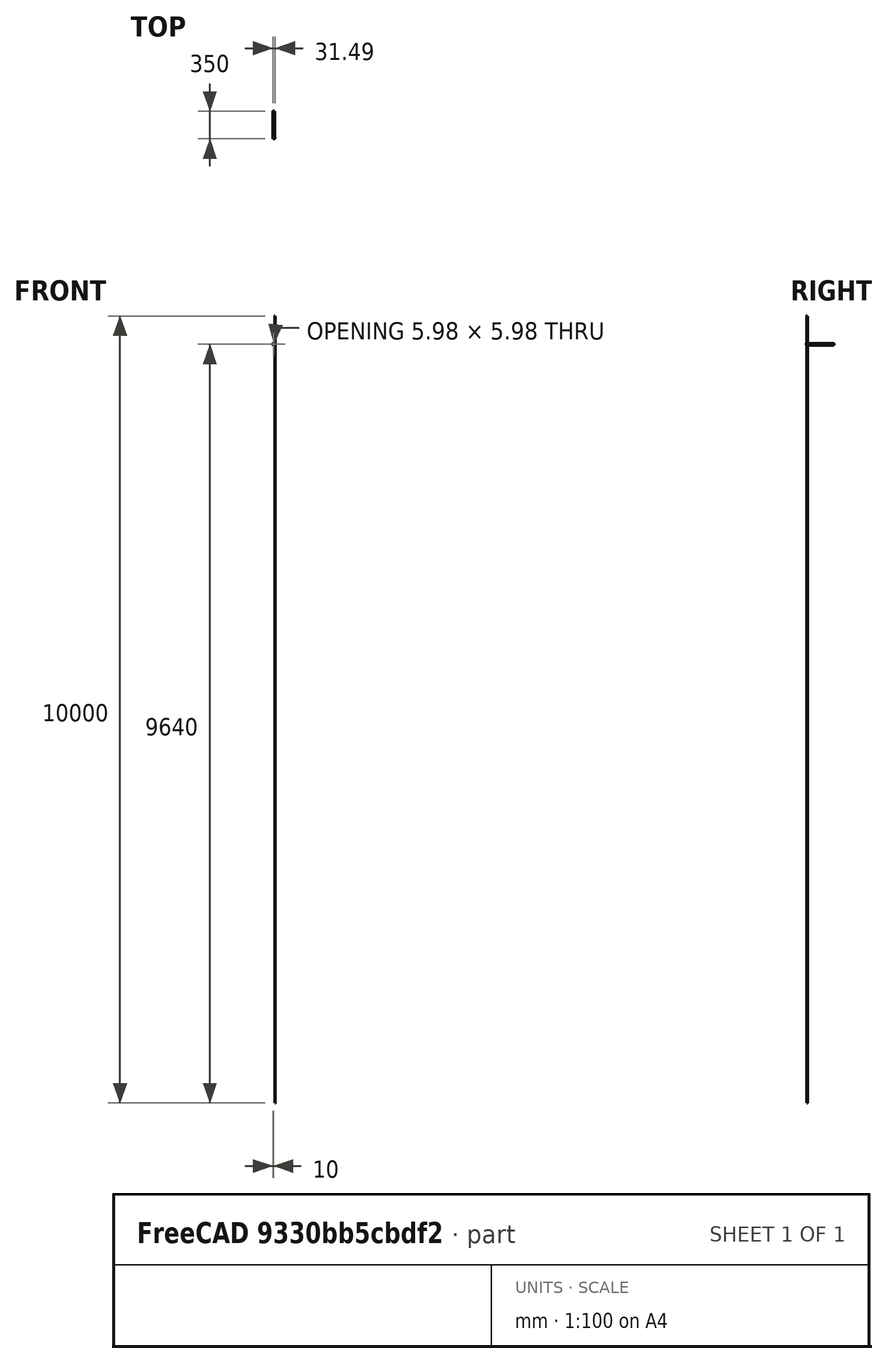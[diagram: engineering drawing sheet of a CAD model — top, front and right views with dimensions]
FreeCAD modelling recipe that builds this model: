
FCSTD DOCUMENT  (FreeCAD 0.14R3703 (Git))
Label: perfiles_horizontales_Y
License: CC-BY 3.0
LicenseURL: http://creativecommons.org/licenses/by/3.0/
objects: Sketcher::SketchObject×2, PartDesign::Pad×1, PartDesign::Pocket×1, Part::Feature×1
note: 7 computed .brp shape members not serialized (recipe doc carries the construction recipe); baked Part::Feature solids carry a one-line shape summary decoded from their .brp

FEATURE [Sketcher::SketchObject] Sketch
  Placement = pos=(0,0,-1.5) rot=(-0.57735,0.57735,0.57735;2.0944rad)
  sketch-geometry (136):
    g0: LineSegment StartX=0 StartY=20 StartZ=0 EndX=4.65 EndY=20 EndZ=0
    g1: ArcOfCircle CenterX=-1e-12 CenterY=18.5 CenterZ=0 NormalX=0 NormalY=0 NormalZ=1 Radius=1.5 StartAngle=1.5708 EndAngle=3.14159
    g2: LineSegment StartX=-1.5 StartY=13.85 StartZ=0 EndX=-1.5 EndY=18.5 EndZ=0
    g3: ArcOfCircle CenterX=-1.3 CenterY=13.85 CenterZ=0 NormalX=0 NormalY=0 NormalZ=1 Radius=0.2 StartAngle=3.14159 EndAngle=4.71239
    g4: LineSegment StartX=-1 StartY=13.65 StartZ=0 EndX=-1.3 EndY=13.65 EndZ=0
    g5: LineSegment StartX=-1 StartY=13.3 StartZ=0 EndX=-1 EndY=13.65 EndZ=0
    g6: ArcOfCircle CenterX=-0.8 CenterY=13.3 CenterZ=0 NormalX=0 NormalY=0 NormalZ=1 Radius=0.2 StartAngle=3.14159 EndAngle=4.71239
    g7: LineSegment StartX=-0.5 StartY=13.1 StartZ=0 EndX=-0.8 EndY=13.1 EndZ=0
    g8: ArcOfCircle CenterX=-0.5 CenterY=13.6 CenterZ=0 NormalX=0 NormalY=0 NormalZ=1 Radius=0.5 StartAngle=4.71239 EndAngle=6.28319
    g9: LineSegment StartX=2.68e-07 StartY=15.5 StartZ=0 EndX=2.68e-07 EndY=13.6 EndZ=0
    g10: ArcOfCircle CenterX=0.5 CenterY=15.5 CenterZ=0 NormalX=0 NormalY=0 NormalZ=1 Radius=0.5 StartAngle=1.5708 EndAngle=3.14159
    g11: LineSegment StartX=1.23223 StartY=16 StartZ=0 EndX=0.5 EndY=16 EndZ=0
    g12: ArcOfCircle CenterX=1.23223 CenterY=15.5 CenterZ=0 NormalX=0 NormalY=0 NormalZ=1 Radius=0.5 StartAngle=0.785398 EndAngle=1.5708
    g13: LineSegment StartX=3.85355 StartY=13.5858 StartZ=0 EndX=1.58579 EndY=15.8536 EndZ=0
    g14: ArcOfCircle CenterX=3.5 CenterY=13.2322 CenterZ=0 NormalX=0 NormalY=0 NormalZ=1 Radius=0.5 StartAngle=0 EndAngle=0.785398
    g15: LineSegment StartX=4 StartY=10.9536 StartZ=0 EndX=4 EndY=13.2322 EndZ=0
    g16: ArcOfCircle CenterX=4.2 CenterY=10.9536 CenterZ=0 NormalX=0 NormalY=0 NormalZ=1 Radius=0.2 StartAngle=3.14159 EndAngle=3.66519
    g17: LineSegment StartX=4.46188 StartY=10.1 StartZ=0 EndX=4.0268 EndY=10.8536 EndZ=0
    g18: ArcOfCircle CenterX=4.28868 CenterY=10 CenterZ=0 NormalX=0 NormalY=0 NormalZ=1 Radius=0.2 StartAngle=5.75959 EndAngle=6.80678
    g19: LineSegment StartX=4.0268 StartY=9.14641 StartZ=0 EndX=4.46188 EndY=9.9 EndZ=0
    g20: ArcOfCircle CenterX=4.2 CenterY=9.04641 CenterZ=0 NormalX=0 NormalY=0 NormalZ=1 Radius=0.2 StartAngle=2.61799 EndAngle=3.14159
    g21: LineSegment StartX=4 StartY=6.76777 StartZ=0 EndX=4 EndY=9.04641 EndZ=0
    g22: ArcOfCircle CenterX=3.5 CenterY=6.76777 CenterZ=0 NormalX=0 NormalY=0 NormalZ=1 Radius=0.5 StartAngle=5.49779 EndAngle=6.28319
    g23: LineSegment StartX=1.58579 StartY=4.14645 StartZ=0 EndX=3.85355 EndY=6.41421 EndZ=0
    g24: ArcOfCircle CenterX=1.23223 CenterY=4.5 CenterZ=0 NormalX=0 NormalY=0 NormalZ=1 Radius=0.5 StartAngle=4.71239 EndAngle=5.49779
    g25: LineSegment StartX=0.5 StartY=4 StartZ=0 EndX=1.23223 EndY=4 EndZ=0
    g26: ArcOfCircle CenterX=0.5 CenterY=4.5 CenterZ=0 NormalX=0 NormalY=0 NormalZ=1 Radius=0.5 StartAngle=3.14159 EndAngle=4.71239
    g27: LineSegment StartX=2.68e-07 StartY=6.4 StartZ=0 EndX=2.68e-07 EndY=4.5 EndZ=0
    g28: ArcOfCircle CenterX=-0.5 CenterY=6.4 CenterZ=0 NormalX=0 NormalY=0 NormalZ=1 Radius=0.5 StartAngle=0 EndAngle=1.5708
    g29: LineSegment StartX=-0.8 StartY=6.9 StartZ=0 EndX=-0.5 EndY=6.9 EndZ=0
    g30: ArcOfCircle CenterX=-0.8 CenterY=6.7 CenterZ=0 NormalX=0 NormalY=0 NormalZ=1 Radius=0.2 StartAngle=1.5708 EndAngle=3.14159
    g31: LineSegment StartX=-1 StartY=6.35 StartZ=0 EndX=-1 EndY=6.7 EndZ=0
    g32: LineSegment StartX=-1.3 StartY=6.35 StartZ=0 EndX=-1 EndY=6.35 EndZ=0
    g33: ArcOfCircle CenterX=-1.3 CenterY=6.15 CenterZ=0 NormalX=0 NormalY=0 NormalZ=1 Radius=0.2 StartAngle=1.5708 EndAngle=3.14159
    g34: LineSegment StartX=-1.5 StartY=1.5 StartZ=0 EndX=-1.5 EndY=6.15 EndZ=0
    g35: ArcOfCircle CenterX=0 CenterY=1.5 CenterZ=0 NormalX=0 NormalY=0 NormalZ=1 Radius=1.5 StartAngle=3.14159 EndAngle=4.71239
    g36: LineSegment StartX=4.65 StartY=1e-12 StartZ=0 EndX=0 EndY=0 EndZ=0
    g37: ArcOfCircle CenterX=4.65 CenterY=0.2 CenterZ=0 NormalX=0 NormalY=0 NormalZ=1 Radius=0.2 StartAngle=4.71239 EndAngle=6.28319
    g38: LineSegment StartX=4.85 StartY=0.5 StartZ=0 EndX=4.85 EndY=0.2 EndZ=0
    g39: LineSegment StartX=5.2 StartY=0.5 StartZ=0 EndX=4.85 EndY=0.5 EndZ=0
    g40: ArcOfCircle CenterX=5.2 CenterY=0.7 CenterZ=0 NormalX=0 NormalY=0 NormalZ=1 Radius=0.2 StartAngle=4.71239 EndAngle=6.28319
    g41: LineSegment StartX=5.4 StartY=1 StartZ=0 EndX=5.4 EndY=0.7 EndZ=0
    g42: ArcOfCircle CenterX=4.9 CenterY=1 CenterZ=0 NormalX=0 NormalY=0 NormalZ=1 Radius=0.5 StartAngle=0 EndAngle=1.5708
    g43: LineSegment StartX=3 StartY=1.5 StartZ=0 EndX=4.9 EndY=1.5 EndZ=0
    g44: ArcOfCircle CenterX=3 CenterY=2 CenterZ=0 NormalX=0 NormalY=0 NormalZ=1 Radius=0.5 StartAngle=3.14159 EndAngle=4.71239
    g45: LineSegment StartX=2.5 StartY=2.73223 StartZ=0 EndX=2.5 EndY=2 EndZ=0
    g46: ArcOfCircle CenterX=3 CenterY=2.73223 CenterZ=0 NormalX=0 NormalY=0 NormalZ=1 Radius=0.5 StartAngle=2.35619 EndAngle=3.14159
    g47: LineSegment StartX=4.91421 StartY=5.35355 StartZ=0 EndX=2.64645 EndY=3.08579 EndZ=0
    g48: ArcOfCircle CenterX=5.26777 CenterY=5 CenterZ=0 NormalX=0 NormalY=0 NormalZ=1 Radius=0.5 StartAngle=1.5708 EndAngle=2.35619
    g49: LineSegment StartX=7.54641 StartY=5.5 StartZ=0 EndX=5.26777 EndY=5.5 EndZ=0
    g50: ArcOfCircle CenterX=7.54641 CenterY=5.7 CenterZ=0 NormalX=0 NormalY=0 NormalZ=1 Radius=0.2 StartAngle=4.71239 EndAngle=5.23599
    g51: LineSegment StartX=8.4 StartY=5.96188 StartZ=0 EndX=7.64641 EndY=5.52679 EndZ=0
    g52: ArcOfCircle CenterX=8.5 CenterY=5.78868 CenterZ=0 NormalX=0 NormalY=0 NormalZ=1 Radius=0.2 StartAngle=1.0472 EndAngle=2.0944
    g53: LineSegment StartX=9.35359 StartY=5.52679 StartZ=0 EndX=8.6 EndY=5.96188 EndZ=0
    g54: ArcOfCircle CenterX=9.45359 CenterY=5.7 CenterZ=0 NormalX=0 NormalY=0 NormalZ=1 Radius=0.2 StartAngle=4.18879 EndAngle=4.71239
    g55: LineSegment StartX=11.7322 StartY=5.5 StartZ=0 EndX=9.45359 EndY=5.5 EndZ=0
    g56: ArcOfCircle CenterX=11.7322 CenterY=5 CenterZ=0 NormalX=0 NormalY=0 NormalZ=1 Radius=0.5 StartAngle=0.785398 EndAngle=1.5708
    g57: LineSegment StartX=14.3536 StartY=3.08579 StartZ=0 EndX=12.0858 EndY=5.35355 EndZ=0
    g58: ArcOfCircle CenterX=14 CenterY=2.73223 CenterZ=0 NormalX=0 NormalY=0 NormalZ=1 Radius=0.5 StartAngle=0 EndAngle=0.785398
    g59: LineSegment StartX=14.5 StartY=2 StartZ=0 EndX=14.5 EndY=2.73223 EndZ=0
    g60: ArcOfCircle CenterX=14 CenterY=2 CenterZ=0 NormalX=0 NormalY=0 NormalZ=1 Radius=0.5 StartAngle=4.71239 EndAngle=6.28319
    g61: LineSegment StartX=12.1 StartY=1.5 StartZ=0 EndX=14 EndY=1.5 EndZ=0
    g62: ArcOfCircle CenterX=12.1 CenterY=1 CenterZ=0 NormalX=0 NormalY=0 NormalZ=1 Radius=0.5 StartAngle=1.5708 EndAngle=3.14159
    g63: LineSegment StartX=11.6 StartY=0.7 StartZ=0 EndX=11.6 EndY=1 EndZ=0
    g64: ArcOfCircle CenterX=11.8 CenterY=0.7 CenterZ=0 NormalX=0 NormalY=0 NormalZ=1 Radius=0.2 StartAngle=3.14159 EndAngle=4.71239
    g65: LineSegment StartX=12.15 StartY=0.5 StartZ=0 EndX=11.8 EndY=0.5 EndZ=0
    g66: LineSegment StartX=12.15 StartY=0.2 StartZ=0 EndX=12.15 EndY=0.5 EndZ=0
    g67: ArcOfCircle CenterX=12.35 CenterY=0.2 CenterZ=0 NormalX=0 NormalY=0 NormalZ=1 Radius=0.2 StartAngle=3.14159 EndAngle=4.71239
    g68: LineSegment StartX=17 StartY=1e-12 StartZ=0 EndX=12.35 EndY=0 EndZ=0
    g69: ArcOfCircle CenterX=17 CenterY=1.5 CenterZ=0 NormalX=0 NormalY=0 NormalZ=1 Radius=1.5 StartAngle=4.71239 EndAngle=6.28319
    g70: LineSegment StartX=18.5 StartY=6.15 StartZ=0 EndX=18.5 EndY=1.5 EndZ=0
    g71: ArcOfCircle CenterX=18.3 CenterY=6.15 CenterZ=0 NormalX=0 NormalY=0 NormalZ=1 Radius=0.2 StartAngle=0 EndAngle=1.5708
    g72: LineSegment StartX=18 StartY=6.35 StartZ=0 EndX=18.3 EndY=6.35 EndZ=0
    g73: LineSegment StartX=18 StartY=6.7 StartZ=0 EndX=18 EndY=6.35 EndZ=0
    g74: ArcOfCircle CenterX=17.8 CenterY=6.7 CenterZ=0 NormalX=0 NormalY=0 NormalZ=1 Radius=0.2 StartAngle=0 EndAngle=1.5708
    g75: LineSegment StartX=17.5 StartY=6.9 StartZ=0 EndX=17.8 EndY=6.9 EndZ=0
    g76: ArcOfCircle CenterX=17.5 CenterY=6.4 CenterZ=0 NormalX=0 NormalY=0 NormalZ=1 Radius=0.5 StartAngle=1.5708 EndAngle=3.14159
    g77: LineSegment StartX=17 StartY=4.5 StartZ=0 EndX=17 EndY=6.4 EndZ=0
    g78: ArcOfCircle CenterX=16.5 CenterY=4.5 CenterZ=0 NormalX=0 NormalY=0 NormalZ=1 Radius=0.5 StartAngle=4.71239 EndAngle=6.28319
    g79: LineSegment StartX=15.7678 StartY=4 StartZ=0 EndX=16.5 EndY=4 EndZ=0
    g80: ArcOfCircle CenterX=15.7678 CenterY=4.5 CenterZ=0 NormalX=0 NormalY=0 NormalZ=1 Radius=0.5 StartAngle=3.92699 EndAngle=4.71239
    g81: LineSegment StartX=13.1464 StartY=6.41421 StartZ=0 EndX=15.4142 EndY=4.14645 EndZ=0
    g82: ArcOfCircle CenterX=13.5 CenterY=6.76777 CenterZ=0 NormalX=0 NormalY=0 NormalZ=1 Radius=0.5 StartAngle=3.14159 EndAngle=3.92699
    g83: LineSegment StartX=13 StartY=9.04641 StartZ=0 EndX=13 EndY=6.76777 EndZ=0
    g84: ArcOfCircle CenterX=12.8 CenterY=9.04641 CenterZ=0 NormalX=0 NormalY=0 NormalZ=1 Radius=0.2 StartAngle=0 EndAngle=0.523599
    g85: LineSegment StartX=12.5381 StartY=9.9 StartZ=0 EndX=12.9732 EndY=9.14641 EndZ=0
    g86: ArcOfCircle CenterX=12.7113 CenterY=10 CenterZ=0 NormalX=0 NormalY=0 NormalZ=1 Radius=0.2 StartAngle=2.61799 EndAngle=3.66519
    g87: LineSegment StartX=12.9732 StartY=10.8536 StartZ=0 EndX=12.5381 EndY=10.1 EndZ=0
    g88: ArcOfCircle CenterX=12.8 CenterY=10.9536 CenterZ=0 NormalX=0 NormalY=0 NormalZ=1 Radius=0.2 StartAngle=5.75959 EndAngle=6.28319
    g89: LineSegment StartX=13 StartY=13.2322 StartZ=0 EndX=13 EndY=10.9536 EndZ=0
    g90: ArcOfCircle CenterX=13.5 CenterY=13.2322 CenterZ=0 NormalX=0 NormalY=0 NormalZ=1 Radius=0.5 StartAngle=2.35619 EndAngle=3.14159
    g91: LineSegment StartX=15.4142 StartY=15.8536 StartZ=0 EndX=13.1464 EndY=13.5858 EndZ=0
    g92: ArcOfCircle CenterX=15.7678 CenterY=15.5 CenterZ=0 NormalX=0 NormalY=0 NormalZ=1 Radius=0.5 StartAngle=1.5708 EndAngle=2.35619
    g93: LineSegment StartX=16.5 StartY=16 StartZ=0 EndX=15.7678 EndY=16 EndZ=0
    g94: ArcOfCircle CenterX=16.5 CenterY=15.5 CenterZ=0 NormalX=0 NormalY=0 NormalZ=1 Radius=0.5 StartAngle=0 EndAngle=1.5708
    g95: LineSegment StartX=17 StartY=13.6 StartZ=0 EndX=17 EndY=15.5 EndZ=0
    g96: ArcOfCircle CenterX=17.5 CenterY=13.6 CenterZ=0 NormalX=0 NormalY=0 NormalZ=1 Radius=0.5 StartAngle=3.14159 EndAngle=4.71239
    g97: LineSegment StartX=17.8 StartY=13.1 StartZ=0 EndX=17.5 EndY=13.1 EndZ=0
    g98: ArcOfCircle CenterX=17.8 CenterY=13.3 CenterZ=0 NormalX=0 NormalY=0 NormalZ=1 Radius=0.2 StartAngle=4.71239 EndAngle=6.28319
    g99: LineSegment StartX=18 StartY=13.65 StartZ=0 EndX=18 EndY=13.3 EndZ=0
    g100: LineSegment StartX=18.3 StartY=13.65 StartZ=0 EndX=18 EndY=13.65 EndZ=0
    g101: ArcOfCircle CenterX=18.3 CenterY=13.85 CenterZ=0 NormalX=0 NormalY=0 NormalZ=1 Radius=0.2 StartAngle=4.71239 EndAngle=6.28319
    g102: LineSegment StartX=18.5 StartY=18.5 StartZ=0 EndX=18.5 EndY=13.85 EndZ=0
    g103: ArcOfCircle CenterX=17 CenterY=18.5 CenterZ=0 NormalX=0 NormalY=0 NormalZ=1 Radius=1.5 StartAngle=0 EndAngle=1.5708
    g104: LineSegment StartX=12.35 StartY=20 StartZ=0 EndX=17 EndY=20 EndZ=0
    g105: ArcOfCircle CenterX=12.35 CenterY=19.8 CenterZ=0 NormalX=0 NormalY=0 NormalZ=1 Radius=0.2 StartAngle=1.5708 EndAngle=3.14159
    g106: LineSegment StartX=12.15 StartY=19.5 StartZ=0 EndX=12.15 EndY=19.8 EndZ=0
    g107: LineSegment StartX=11.8 StartY=19.5 StartZ=0 EndX=12.15 EndY=19.5 EndZ=0
    g108: ArcOfCircle CenterX=11.8 CenterY=19.3 CenterZ=0 NormalX=0 NormalY=0 NormalZ=1 Radius=0.2 StartAngle=1.5708 EndAngle=3.14159
    g109: LineSegment StartX=11.6 StartY=19 StartZ=0 EndX=11.6 EndY=19.3 EndZ=0
    g110: ArcOfCircle CenterX=12.1 CenterY=19 CenterZ=0 NormalX=0 NormalY=0 NormalZ=1 Radius=0.5 StartAngle=3.14159 EndAngle=4.71239
    g111: LineSegment StartX=14 StartY=18.5 StartZ=0 EndX=12.1 EndY=18.5 EndZ=0
    g112: ArcOfCircle CenterX=14 CenterY=18 CenterZ=0 NormalX=0 NormalY=0 NormalZ=1 Radius=0.5 StartAngle=0 EndAngle=1.5708
    g113: LineSegment StartX=14.5 StartY=17.2678 StartZ=0 EndX=14.5 EndY=18 EndZ=0
    g114: ArcOfCircle CenterX=14 CenterY=17.2678 CenterZ=0 NormalX=0 NormalY=0 NormalZ=1 Radius=0.5 StartAngle=5.49779 EndAngle=6.28319
    g115: LineSegment StartX=12.0858 StartY=14.6464 StartZ=0 EndX=14.3536 EndY=16.9142 EndZ=0
    g116: ArcOfCircle CenterX=11.7322 CenterY=15 CenterZ=0 NormalX=0 NormalY=0 NormalZ=1 Radius=0.5 StartAngle=4.71239 EndAngle=5.49779
    g117: LineSegment StartX=9.45359 StartY=14.5 StartZ=0 EndX=11.7322 EndY=14.5 EndZ=0
    g118: ArcOfCircle CenterX=9.45359 CenterY=14.3 CenterZ=0 NormalX=0 NormalY=0 NormalZ=1 Radius=0.2 StartAngle=1.5708 EndAngle=2.0944
    g119: LineSegment StartX=8.6 StartY=14.0381 StartZ=0 EndX=9.35359 EndY=14.4732 EndZ=0
    g120: ArcOfCircle CenterX=8.5 CenterY=14.2113 CenterZ=0 NormalX=0 NormalY=0 NormalZ=1 Radius=0.2 StartAngle=4.18879 EndAngle=5.23599
    g121: LineSegment StartX=7.64641 StartY=14.4732 StartZ=0 EndX=8.4 EndY=14.0381 EndZ=0
    g122: ArcOfCircle CenterX=7.54641 CenterY=14.3 CenterZ=0 NormalX=0 NormalY=0 NormalZ=1 Radius=0.2 StartAngle=1.0472 EndAngle=1.5708
    g123: LineSegment StartX=5.26777 StartY=14.5 StartZ=0 EndX=7.54641 EndY=14.5 EndZ=0
    g124: ArcOfCircle CenterX=5.26777 CenterY=15 CenterZ=0 NormalX=0 NormalY=0 NormalZ=1 Radius=0.5 StartAngle=3.92699 EndAngle=4.71239
    g125: LineSegment StartX=2.64645 StartY=16.9142 StartZ=0 EndX=4.91421 EndY=14.6464 EndZ=0
    g126: ArcOfCircle CenterX=3 CenterY=17.2678 CenterZ=0 NormalX=0 NormalY=0 NormalZ=1 Radius=0.5 StartAngle=3.14159 EndAngle=3.92699
    g127: LineSegment StartX=2.5 StartY=18 StartZ=0 EndX=2.5 EndY=17.2678 EndZ=0
    g128: ArcOfCircle CenterX=3 CenterY=18 CenterZ=0 NormalX=0 NormalY=0 NormalZ=1 Radius=0.5 StartAngle=1.5708 EndAngle=3.14159
    g129: LineSegment StartX=4.9 StartY=18.5 StartZ=0 EndX=3 EndY=18.5 EndZ=0
    g130: ArcOfCircle CenterX=4.9 CenterY=19 CenterZ=0 NormalX=0 NormalY=0 NormalZ=1 Radius=0.5 StartAngle=4.71239 EndAngle=6.28319
    g131: LineSegment StartX=5.4 StartY=19.3 StartZ=0 EndX=5.4 EndY=19 EndZ=0
    g132: ArcOfCircle CenterX=5.2 CenterY=19.3 CenterZ=0 NormalX=0 NormalY=0 NormalZ=1 Radius=0.2 StartAngle=0 EndAngle=1.5708
    g133: LineSegment StartX=4.85 StartY=19.5 StartZ=0 EndX=5.2 EndY=19.5 EndZ=0
    g134: LineSegment StartX=4.85 StartY=19.8 StartZ=0 EndX=4.85 EndY=19.5 EndZ=0
    g135: ArcOfCircle CenterX=4.65 CenterY=19.8 CenterZ=0 NormalX=0 NormalY=0 NormalZ=1 Radius=0.2 StartAngle=0 EndAngle=1.5708
  constraints (136):
    c: Coincident(g0,g1)
    c: Coincident(g135,g0)
    c: Coincident(g1,g2)
    c: Coincident(g2,g3)
    c: Coincident(g3,g4)
    c: Coincident(g4,g5)
    c: Coincident(g6,g5)
    c: Coincident(g7,g6)
    c: Coincident(g8,g7)
    c: Coincident(g9,g8)
    c: Coincident(g10,g9)
    c: Coincident(g10,g11)
    c: Coincident(g11,g12)
    c: Coincident(g12,g13)
    c: Coincident(g14,g13)
    c: Coincident(g15,g14)
    c: Coincident(g15,g16)
    c: Coincident(g16,g17)
    c: Coincident(g17,g18)
    c: Coincident(g18,g19)
    c: Coincident(g19,g20)
    c: Coincident(g20,g21)
    c: Coincident(g21,g22)
    c: Coincident(g22,g23)
    c: Coincident(g23,g24)
    c: Coincident(g24,g25)
    c: Coincident(g26,g25)
    c: Coincident(g26,g27)
    c: Coincident(g28,g27)
    c: Coincident(g28,g29)
    c: Coincident(g30,g29)
    c: Coincident(g31,g30)
    c: Coincident(g31,g32)
    c: Coincident(g32,g33)
    c: Coincident(g33,g34)
    c: Coincident(g35,g34)
    c: Coincident(g36,g35)
    c: Coincident(g37,g36)
    c: Coincident(g37,g38)
    c: Coincident(g38,g39)
    c: Coincident(g40,g39)
    c: Coincident(g40,g41)
    c: Coincident(g41,g42)
    c: Coincident(g43,g42)
    c: Coincident(g44,g43)
    c: Coincident(g44,g45)
    c: Coincident(g45,g46)
    c: Coincident(g46,g47)
    c: Coincident(g47,g48)
    c: Coincident(g49,g48)
    c: Coincident(g49,g50)
    c: Coincident(g50,g51)
    c: Coincident(g51,g52)
    c: Coincident(g53,g52)
    c: Coincident(g54,g53)
    c: Coincident(g55,g54)
    c: Coincident(g56,g55)
    c: Coincident(g56,g57)
    c: Coincident(g58,g57)
    c: Coincident(g59,g58)
    c: Coincident(g60,g59)
    c: Coincident(g61,g60)
    c: Coincident(g62,g61)
    c: Coincident(g62,g63)
    c: Coincident(g64,g63)
    c: Coincident(g65,g64)
    c: Coincident(g66,g65)
    c: Coincident(g67,g66)
    c: Coincident(g67,g68)
    c: Coincident(g69,g68)
    c: Coincident(g70,g69)
    c: Coincident(g71,g70)
    c: Coincident(g72,g71)
    c: Coincident(g73,g72)
    c: Coincident(g73,g74)
    c: Coincident(g75,g74)
    c: Coincident(g76,g75)
    c: Coincident(g76,g77)
    c: Coincident(g77,g78)
    c: Coincident(g78,g79)
    c: Coincident(g80,g79)
    c: Coincident(g81,g80)
    c: Coincident(g81,g82)
    c: Coincident(g82,g83)
    c: Coincident(g83,g84)
    c: Coincident(g85,g84)
    c: Coincident(g86,g85)
    c: Coincident(g86,g87)
    c: Coincident(g88,g87)
    c: Coincident(g88,g89)
    c: Coincident(g89,g90)
    c: Coincident(g91,g90)
    c: Coincident(g92,g91)
    c: Coincident(g93,g92)
    c: Coincident(g94,g93)
    c: Coincident(g94,g95)
    c: Coincident(g95,g96)
    c: Coincident(g96,g97)
    c: Coincident(g98,g97)
    c: Coincident(g98,g99)
    c: Coincident(g100,g99)
    c: Coincident(g100,g101)
    c: Coincident(g101,g102)
    c: Coincident(g102,g103)
    c: Coincident(g103,g104)
    c: Coincident(g104,g105)
    c: Coincident(g106,g105)
    c: Coincident(g107,g106)
    c: Coincident(g108,g107)
    c: Coincident(g109,g108)
    c: Coincident(g110,g109)
    c: Coincident(g111,g110)
    c: Coincident(g112,g111)
    c: Coincident(g112,g113)
    c: Coincident(g113,g114)
    c: Coincident(g114,g115)
    c: Coincident(g115,g116)
    c: Coincident(g117,g116)
    c: Coincident(g118,g117)
    c: Coincident(g119,g118)
    c: Coincident(g119,g120)
    c: Coincident(g121,g120)
    c: Coincident(g121,g122)
    c: Coincident(g122,g123)
    c: Coincident(g124,g123)
    c: Coincident(g124,g125)
    c: Coincident(g126,g125)
    c: Coincident(g127,g126)
    c: Coincident(g128,g127)
    c: Coincident(g129,g128)
    c: Coincident(g130,g129)
    c: Coincident(g130,g131)
    c: Coincident(g131,g132)
    c: Coincident(g133,g132)
    c: Coincident(g134,g133)
    c: Coincident(g135,g134)
FEATURE [PartDesign::Pad] Pad
  Length = 350
  Length2 = 100
  Placement = pos=(0,0,-1.5) rot=(-0.57735,0.57735,0.57735;2.0944rad)
  Sketch = -> Sketch
  Type = 0
FEATURE [Sketcher::SketchObject] Sketch001
  Placement = pos=(0,350,-1.5) rot=(-0.57735,0.57735,0.57735;2.0944rad)
  Support = -> Pad [Face138]
  sketch-geometry (16):
    g0: ArcOfCircle CenterX=8.5 CenterY=10 CenterZ=0 NormalX=0 NormalY=0 NormalZ=1 Radius=3.54978 StartAngle=2.14023 EndAngle=2.57348
    g1: LineSegment StartX=6.5861 StartY=12.9896 StartZ=0 EndX=7.24181 EndY=12.4453 EndZ=0
    g2: ArcOfCircle CenterX=8.5 CenterY=10 CenterZ=0 NormalX=0 NormalY=0 NormalZ=1 Radius=2.75 StartAngle=1.09559 EndAngle=2.046
    g3: LineSegment StartX=9.75819 StartY=12.4453 StartZ=0 EndX=10.4139 EndY=12.9896 EndZ=0
    g4: ArcOfCircle CenterX=8.5 CenterY=10 CenterZ=0 NormalX=0 NormalY=0 NormalZ=1 Radius=3.54978 StartAngle=0.568112 EndAngle=1.00136
    g5: LineSegment StartX=11.4922 StartY=11.9099 StartZ=0 EndX=10.9453 EndY=11.2582 EndZ=0
    g6: ArcOfCircle CenterX=8.5 CenterY=10 CenterZ=0 NormalX=0 NormalY=0 NormalZ=1 Radius=2.75 StartAngle=5.80798 EndAngle=6.75839
    g7: LineSegment StartX=10.9453 StartY=8.74181 StartZ=0 EndX=11.4922 EndY=8.09007 EndZ=0
    g8: ArcOfCircle CenterX=8.5 CenterY=10 CenterZ=0 NormalX=0 NormalY=0 NormalZ=1 Radius=3.54978 StartAngle=5.28183 EndAngle=5.71507
    g9: LineSegment StartX=10.4139 StartY=7.01036 StartZ=0 EndX=9.75819 EndY=7.5547 EndZ=0
    g10: ArcOfCircle CenterX=8.5 CenterY=10 CenterZ=0 NormalX=0 NormalY=0 NormalZ=1 Radius=2.75 StartAngle=4.23718 EndAngle=5.1876
    g11: LineSegment StartX=7.24181 StartY=7.5547 StartZ=0 EndX=6.5861 EndY=7.01036 EndZ=0
    g12: ArcOfCircle CenterX=8.5 CenterY=10 CenterZ=0 NormalX=0 NormalY=0 NormalZ=1 Radius=3.54978 StartAngle=3.7097 EndAngle=4.14295
    g13: LineSegment StartX=5.50783 StartY=8.09007 StartZ=0 EndX=6.0547 EndY=8.74181 EndZ=0
    g14: ArcOfCircle CenterX=8.5 CenterY=10 CenterZ=0 NormalX=0 NormalY=0 NormalZ=1 Radius=2.75 StartAngle=2.66639 EndAngle=3.6168
    g15: LineSegment StartX=6.0547 StartY=11.2582 StartZ=0 EndX=5.50783 EndY=11.9099 EndZ=0
  constraints (16):
    c: Coincident(g0,g1)
    c: Coincident(g15,g0)
    c: Coincident(g1,g2)
    c: Coincident(g3,g2)
    c: Coincident(g4,g3)
    c: Coincident(g4,g5)
    c: Coincident(g6,g5)
    c: Coincident(g7,g6)
    c: Coincident(g8,g7)
    c: Coincident(g9,g8)
    c: Coincident(g10,g9)
    c: Coincident(g11,g10)
    c: Coincident(g12,g11)
    c: Coincident(g13,g12)
    c: Coincident(g14,g13)
    c: Coincident(g15,g14)
FEATURE [PartDesign::Pocket] Pocket
  Length = 5
  Placement = pos=(0,0,-1.5) rot=(-0.57735,0.57735,0.57735;2.0944rad)
  Sketch = -> Sketch001
  Type = 1
FEATURE [Part::Feature] Pocket001  label="perfiles_horizontales_Y"
  Placement = pos=(0,0,-1.5) rot=(-0.57735,0.57735,0.57735;2.0944rad)
  shape: bbox 20 x 350 x 20 mm, 154 faces (baked)
